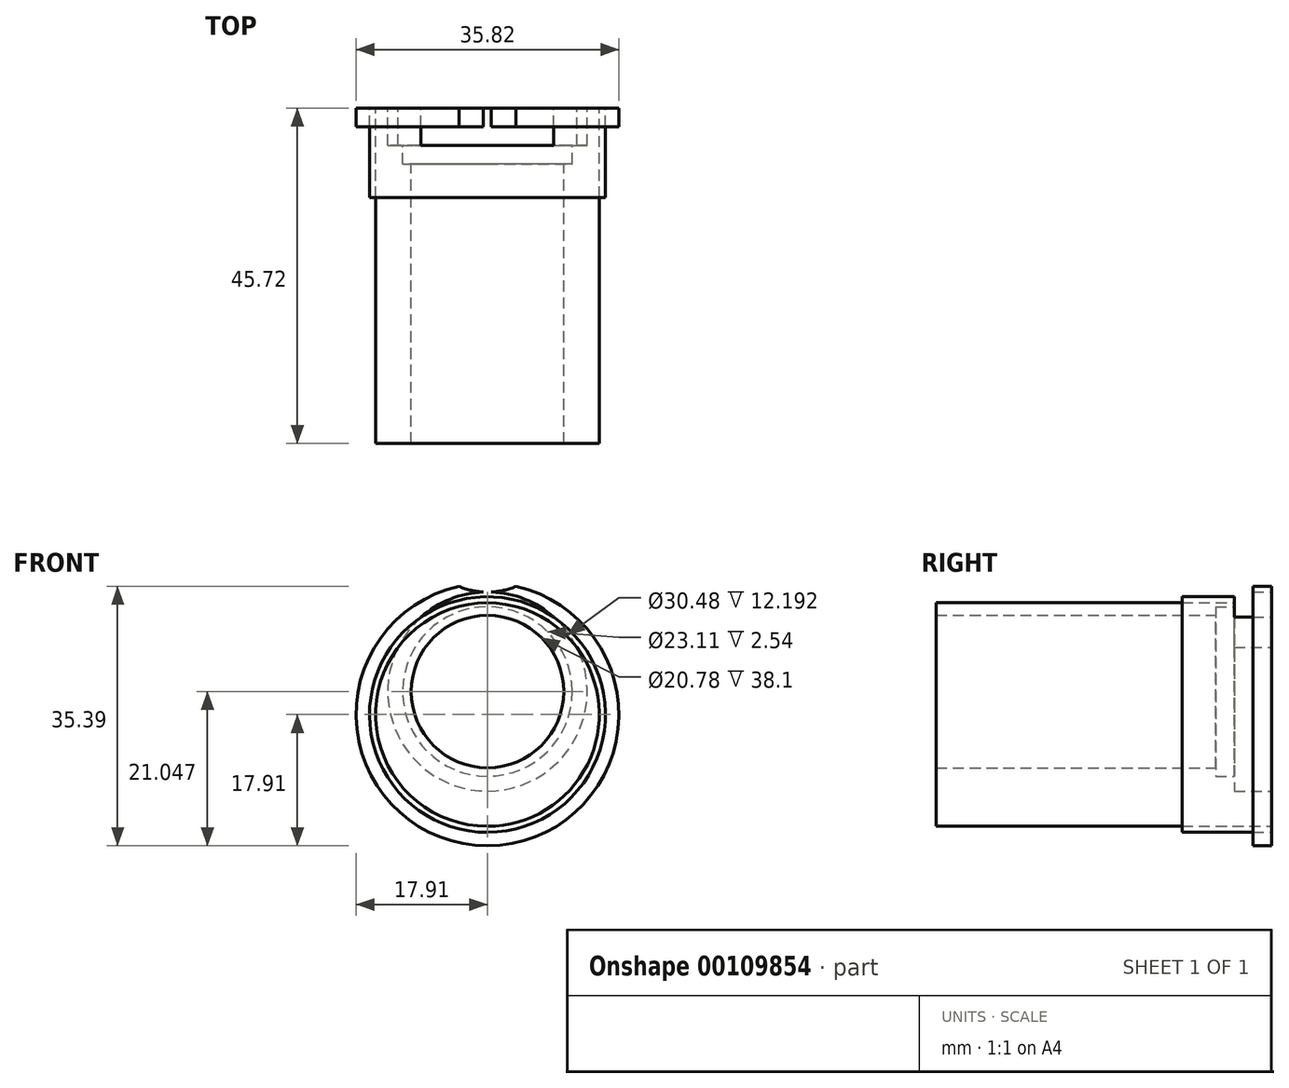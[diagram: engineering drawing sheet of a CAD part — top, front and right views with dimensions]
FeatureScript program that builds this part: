
annotation { "Feature Type Name" : "Feature", "Feature Type Description" : "" }
export const myFeature = defineFeature(function(context is Context, id is Id, definition is map)
    precondition{}
    {
        {
            var Q0;
            Q0=qCreatedBy(makeId("Front.planeOp"),FACE);
            var sketch = newSketch(context, id + "F0", { "sketchPlane" : qUnion([Q0])});
            skCircle(sketch, "E0", {"center": v(0, 0) * mm, "radius": 16.07 * mm});
            skCircle(sketch, "E1", {"center": v(0, 0) * mm, "radius": 15.24 * mm});
            skCircle(sketch, "E2", {"center": v(0, 3.14) * mm, "radius": 10.39 * mm});
            skArc(sketch, "E3", {"start": v(-3.9, 17.48) * mm, "mid": v(0, -17.9) * mm, "end": v(3.9, 17.48) * mm});
            skArc(sketch, "E4", {"start": v(-3.9, 17.48) * mm, "mid": v(0, 16.7) * mm, "end": v(3.9, 17.48) * mm});
            skSolve(sketch);
        }
        {
            var Q0;
            Q0=makeQuery(id+"F0.imprint","IMPRINT",FACE,{"disambiguationData":[TD([[makeQuery(id+"F0.imprint","IMPRINT",EDGE,{"derivedFrom":sQuery(id+"F0.wireOp",EDGE,"E1")}),1.0]])]});
            extrude(context, id + "F1", {"entities" : qUnion([Q0]), "depth" : 45.72 * mm});
        }
        {
            var Q0;
            Q0=makeQuery(id+"F0.imprint","IMPRINT",FACE,{"disambiguationData":[TD([[makeQuery(id+"F0.imprint","IMPRINT",EDGE,{"derivedFrom":sQuery(id+"F0.wireOp",EDGE,"E0")}),-1.0]])]});
            extrude(context, id + "F2", {"entities" : qUnion([Q0]), "depth" : 2.54 * mm});
        }
        {
            var Q0;
            Q0=makeQuery(id+"F0.imprint","IMPRINT",FACE,{"disambiguationData":[TD([[makeQuery(id+"F0.imprint","IMPRINT",EDGE,{"derivedFrom":sQuery(id+"F0.wireOp",EDGE,"E0")}),1.0]])]});
            extrude(context, id + "F3", {"entities" : qUnion([Q0]), "depth" : 12.2 * mm});
        }
        {
            var Q0;
            Q0=makeQuery(id+"F1.opExtrude","CAP_FACE",FACE,{"disambiguationData":[OSD([sQuery(id+"F0.wireOp",EDGE,"E1"),sQuery(id+"F0.wireOp",EDGE,"E2")])],"isStart":true});
            var sketch = newSketch(context, id + "F4", { "sketchPlane" : qUnion([Q0])});
            skCircle(sketch, "E5", {"center": v(0, 3.14) * mm, "radius": 11.56 * mm});
            skCircle(sketch, "E6", {"center": v(0, 3.14) * mm, "radius": 13.59 * mm});
            skSolve(sketch);
        }
        {
            var Q0;
            Q0=makeQuery(id+"F4.imprint","IMPRINT",FACE,{"disambiguationData":[TD([[makeQuery(id+"F4.imprint","IMPRINT",EDGE,{"derivedFrom":sQuery(id+"F4.wireOp",EDGE,"E5")}),1.0]])]});
            extrude(context, id + "F5", {"entities" : qUnion([Q0]), "operationType" : NewBodyOperationType.REMOVE, "oppositeDirection" : true, "depth" : 7.62 * mm});
        }
        {
            var Q0;
            {var subQ0=sQuery(id+"F4.wireOp",EDGE,"E6");var subQ1=makeQuery(id+"F1.opExtrude","CAP_EDGE",EDGE,{"disambiguationData":[OSD([sQuery(id+"F0.wireOp",EDGE,"E1")])],"isStart":true});var subQ2=makeQuery(id+"F4.imprint","INTERSECT",VERTEX,{"disambiguationData":[OD(0.0)],"derivedFrom":[subQ1,subQ0]});Q0=makeQuery(id+"F4.imprint","IMPRINT",FACE,{"disambiguationData":[TD([[makeQuery(id+"F4.imprint","IMPRINT",EDGE,{"disambiguationData":[TD([[subQ2,-1.0]])],"derivedFrom":subQ0}),1.0]])]});}
            var Q1;
            Q1=makeQuery(id+"F4.imprint","IMPRINT",FACE,{"disambiguationData":[TD([[makeQuery(id+"F4.imprint","IMPRINT",EDGE,{"derivedFrom":sQuery(id+"F4.wireOp",EDGE,"E5")}),-1.0]])]});
            extrude(context, id + "F6", {"entities" : qUnion([Q0, Q1]), "operationType" : NewBodyOperationType.REMOVE, "oppositeDirection" : true, "depth" : 5.08 * mm});
        }
        {
            var Q0;
            Q0=makeQuery(id+"F4.imprint","IMPRINT",FACE,{"disambiguationData":[TD([[makeQuery(id+"F4.imprint","IMPRINT",EDGE,{"derivedFrom":sQuery(id+"F4.wireOp",EDGE,"E5")}),-1.0]])]});
            extrude(context, id + "F7", {"entities" : qUnion([Q0]), "operationType" : NewBodyOperationType.REMOVE, "oppositeDirection" : true, "depth" : 2.54 * mm});
        }
    });
